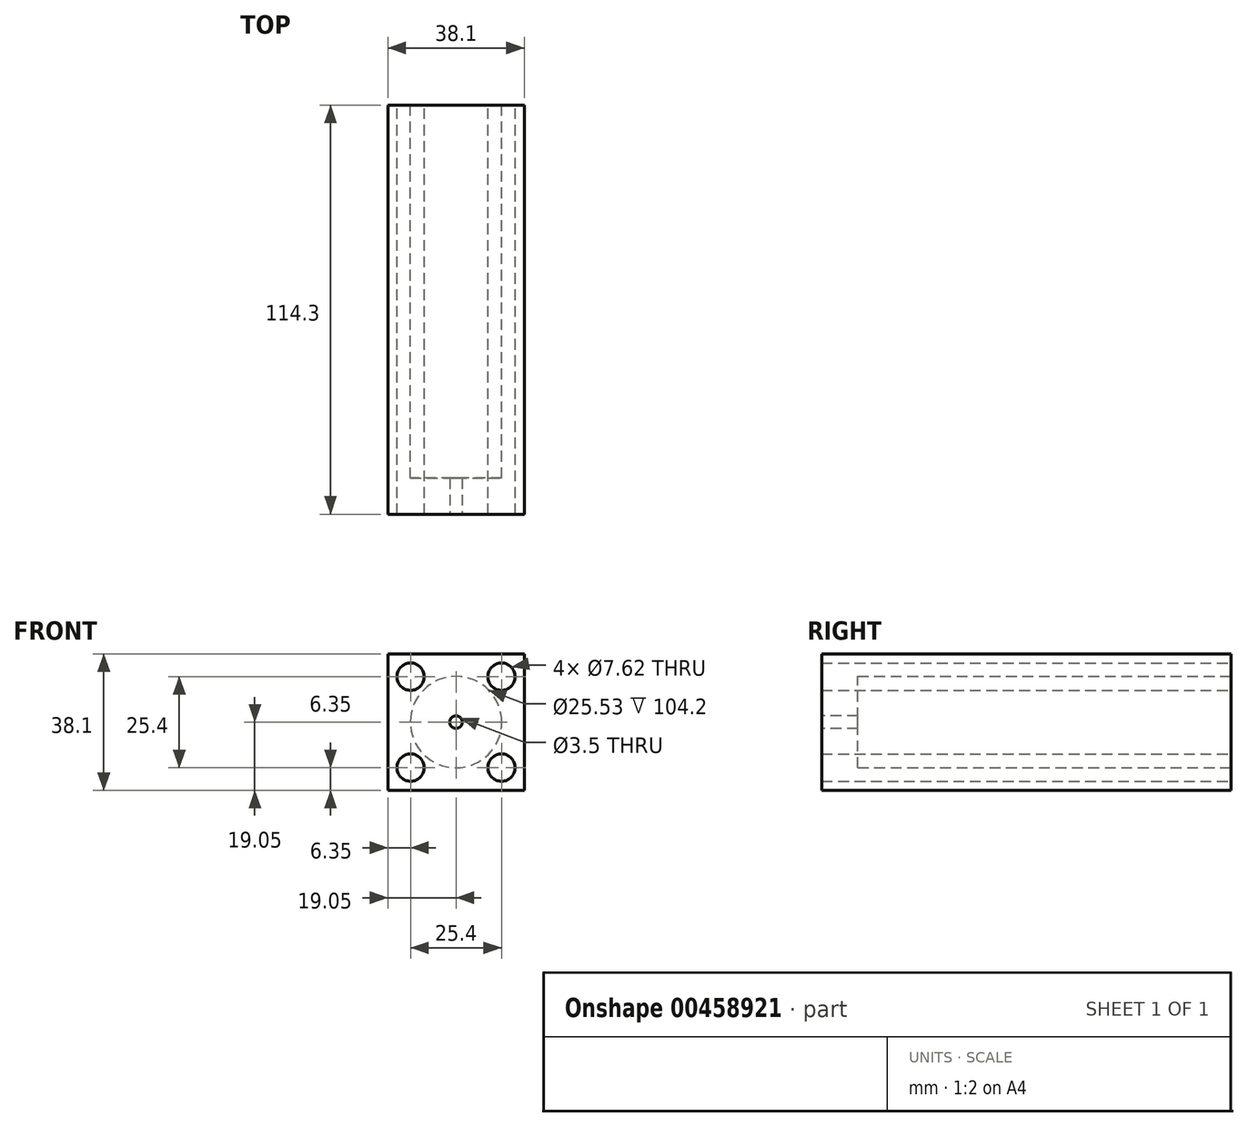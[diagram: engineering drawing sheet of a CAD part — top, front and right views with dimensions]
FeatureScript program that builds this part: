
annotation { "Feature Type Name" : "Feature", "Feature Type Description" : "" }
export const myFeature = defineFeature(function(context is Context, id is Id, definition is map)
    precondition{}
    {
        {
            var Q0;
            Q0=qCreatedBy(makeId("Front.planeOp"),FACE);
            var sketch = newSketch(context, id + "F0", { "sketchPlane" : qUnion([Q0])});
            skLineSegment(sketch, "E0.bottom", {"start": v(19.05, -19.05) * mm, "end": v(-19.05, -19.05) * mm});
            skLineSegment(sketch, "E0.top", {"start": v(19.05, 19.05) * mm, "end": v(-19.05, 19.05) * mm});
            skLineSegment(sketch, "E0.left", {"start": v(19.05, -19.05) * mm, "end": v(19.05, 19.05) * mm});
            skLineSegment(sketch, "E0.right", {"start": v(-19.05, -19.05) * mm, "end": v(-19.05, 19.05) * mm});
            skPoint(sketch, "E0.middle", {"position": v(0, 0) * mm});
            skCircle(sketch, "E1", {"center": v(0, 0) * mm, "radius": 12.76 * mm});
            skCircle(sketch, "E2", {"center": v(-12.7, 12.7) * mm, "radius": 3.81 * mm});
            skCircle(sketch, "E3.MirrorC", {"center": v(-12.7, -12.7) * mm, "radius": 3.81 * mm});
            skCircle(sketch, "E4.MirrorC", {"center": v(12.7, 12.7) * mm, "radius": 3.81 * mm});
            skCircle(sketch, "E5.MirrorC", {"center": v(12.7, -12.7) * mm, "radius": 3.81 * mm});
            skSolve(sketch);
        }
        {
            var Q0;
            Q0=makeQuery(id+"F0.imprint","IMPRINT",FACE,{"disambiguationData":[TD([[makeQuery(id+"F0.imprint","IMPRINT",EDGE,{"derivedFrom":sQuery(id+"F0.wireOp",EDGE,"E0.bottom")}),-1.0]])]});
            extrude(context, id + "F1", {"entities" : qUnion([Q0]), "depth" : 114.3 * mm});
        }
        {
            var Q0;
            Q0=makeQuery(id+"F1.opExtrude","CAP_FACE",FACE,{"disambiguationData":[OSD([sQuery(id+"F0.wireOp",EDGE,"E0.bottom"),sQuery(id+"F0.wireOp",EDGE,"E0.top"),sQuery(id+"F0.wireOp",EDGE,"E0.left"),sQuery(id+"F0.wireOp",EDGE,"E0.right"),sQuery(id+"F0.wireOp",EDGE,"E1"),sQuery(id+"F0.wireOp",EDGE,"E2"),sQuery(id+"F0.wireOp",EDGE,"E3.MirrorC"),sQuery(id+"F0.wireOp",EDGE,"E4.MirrorC"),sQuery(id+"F0.wireOp",EDGE,"E5.MirrorC")])],"isStart":false});
            var sketch = newSketch(context, id + "F2", { "sketchPlane" : qUnion([Q0])});
            skCircle(sketch, "E6.0", {"center": v(0, 0) * mm, "radius": 12.76 * mm});
            skCircle(sketch, "E7", {"center": v(0, 0) * mm, "radius": 1.75 * mm});
            skSolve(sketch);
        }
        {
            var Q0;
            Q0=makeQuery(id+"F2.imprint","IMPRINT",FACE,{"disambiguationData":[TD([[makeQuery(id+"F2.imprint","IMPRINT",EDGE,{"derivedFrom":sQuery(id+"F2.wireOp",EDGE,"E6.0")}),1.0]])]});
            extrude(context, id + "F3", {"entities" : qUnion([Q0]), "operationType" : NewBodyOperationType.ADD, "oppositeDirection" : true, "depth" : 10.1 * mm});
        }
    });
